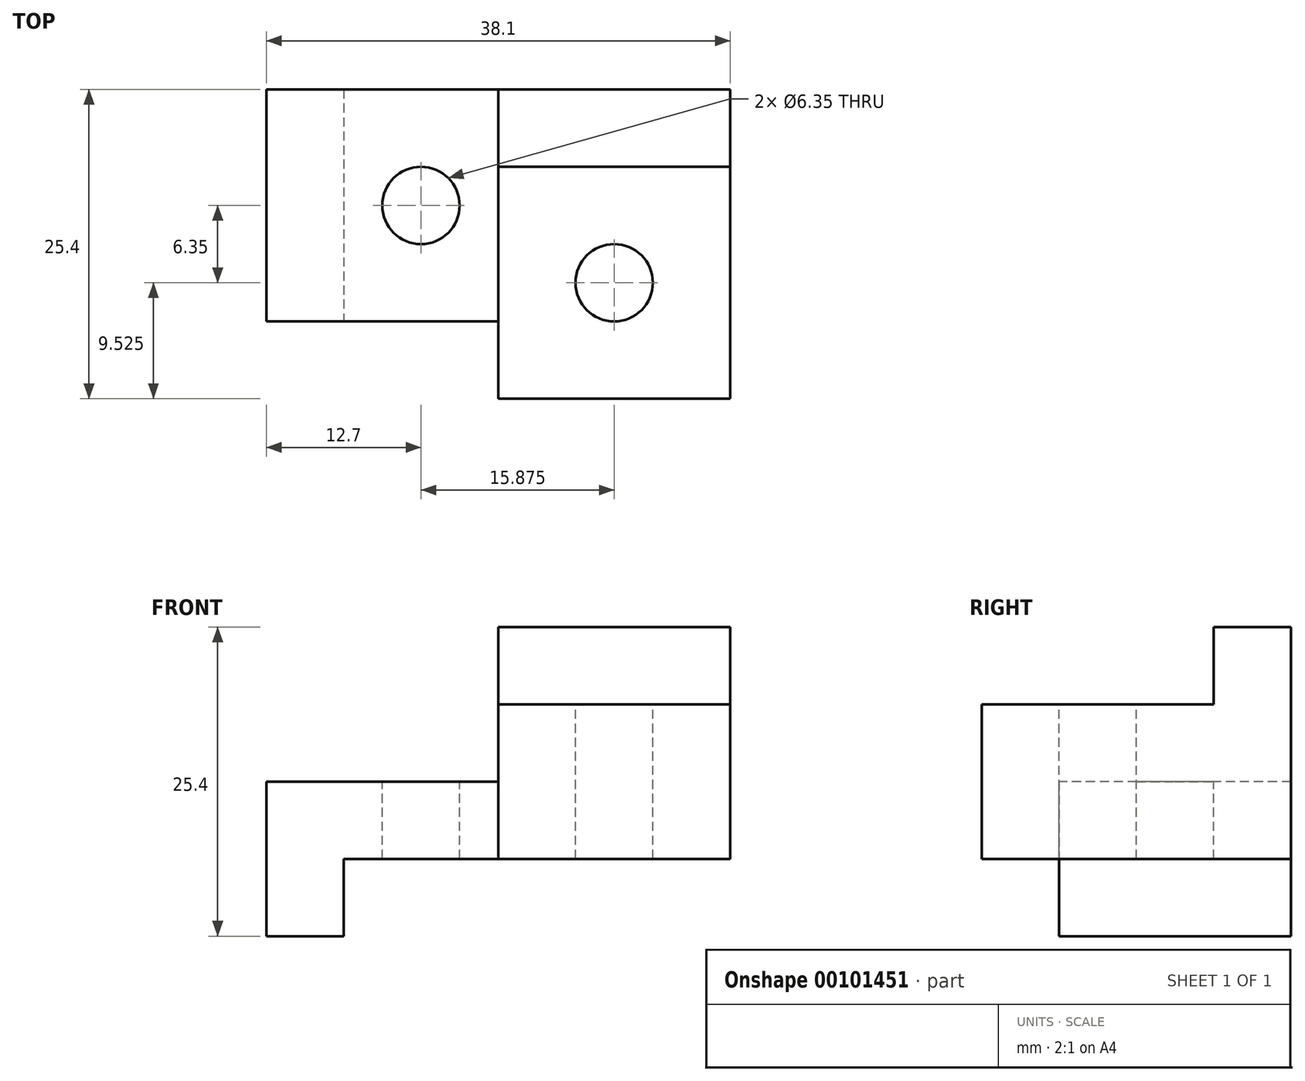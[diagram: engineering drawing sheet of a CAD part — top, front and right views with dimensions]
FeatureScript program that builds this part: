
annotation { "Feature Type Name" : "Feature", "Feature Type Description" : "" }
export const myFeature = defineFeature(function(context is Context, id is Id, definition is map)
    precondition{}
    {
        {
            var Q0;
            Q0=qCreatedBy(makeId("Front.planeOp"),FACE);
            var sketch = newSketch(context, id + "F0", { "sketchPlane" : qUnion([Q0])});
            skLineSegment(sketch, "E0", {"start": v(0, 0) * mm, "end": v(6.35, 0) * mm});
            skLineSegment(sketch, "E1", {"start": v(6.35, 0) * mm, "end": v(6.35, -12.7) * mm});
            skLineSegment(sketch, "E2", {"start": v(6.35, -12.7) * mm, "end": v(0, -12.7) * mm});
            skLineSegment(sketch, "E3", {"start": v(0, -12.7) * mm, "end": v(0, 0) * mm});
            skSolve(sketch);
        }
        {
            var Q0;
            Q0 = qSketchRegion(id + "F0", true);
            extrude(context, id + "F1", {"entities" : qUnion([Q0]), "oppositeDirection" : true, "depth" : 19.05 * mm});
        }
        {
            var Q0;
            Q0=makeQuery(id+"F1.opExtrude","SWEPT_FACE",FACE,{"disambiguationData":[OSD([sQuery(id+"F0.wireOp",EDGE,"E1")])]});
            var sketch = newSketch(context, id + "F2", { "sketchPlane" : qUnion([Q0])});
            skLineSegment(sketch, "E4", {"start": v(19.05, 0) * mm, "end": v(19.05, -6.35) * mm});
            skLineSegment(sketch, "E5", {"start": v(19.05, -6.35) * mm, "end": v(0, -6.35) * mm});
            skLineSegment(sketch, "E6", {"start": v(0, -6.35) * mm, "end": v(0, 0) * mm});
            skLineSegment(sketch, "E7", {"start": v(0, 0) * mm, "end": v(19.05, 0) * mm});
            skSolve(sketch);
        }
        {
            var Q0;
            Q0 = qSketchRegion(id + "F2", true);
            extrude(context, id + "F3", {"entities" : qUnion([Q0]), "operationType" : NewBodyOperationType.ADD, "depth" : 12.7 * mm});
        }
        {
            var Q0;
            Q0=makeQuery(id+"F3.boolean.opBoolean","MERGE",FACE,{"derivedFrom":[makeQuery(id+"F1.opExtrude","SWEPT_FACE",FACE,{"disambiguationData":[OSD([sQuery(id+"F0.wireOp",EDGE,"E0")])]}),makeQuery(id+"F3.opExtrude","SWEPT_FACE",FACE,{"disambiguationData":[OSD([sQuery(id+"F2.wireOp",EDGE,"E7")])]})]});
            var sketch = newSketch(context, id + "F4", { "sketchPlane" : qUnion([Q0])});
            skLineSegment(sketch, "E8", {"start": v(19.05, 19.05) * mm, "end": v(19.05, 9.53) * mm, "construction": true});
            skLineSegment(sketch, "E9", {"start": v(19.05, 9.53) * mm, "end": v(12.7, 9.53) * mm, "construction": true});
            skCircle(sketch, "E10", {"center": v(12.7, 9.53) * mm, "radius": 3.18 * mm});
            skSolve(sketch);
        }
        {
            var Q0;
            Q0 = qSketchRegion(id + "F4", true);
            extrude(context, id + "F5", {"entities" : qUnion([Q0]), "operationType" : NewBodyOperationType.REMOVE, "endBound" : BoundingType.THROUGH_ALL, "oppositeDirection" : true, "depth" : 25.4 * mm});
        }
        {
            var Q0;
            Q0=makeQuery(id+"F3.opExtrude","CAP_FACE",FACE,{"disambiguationData":[OSD([sQuery(id+"F2.wireOp",EDGE,"E4"),sQuery(id+"F2.wireOp",EDGE,"E5"),sQuery(id+"F2.wireOp",EDGE,"E6"),sQuery(id+"F2.wireOp",EDGE,"E7")])],"isStart":false});
            var sketch = newSketch(context, id + "F6", { "sketchPlane" : qUnion([Q0])});
            skLineSegment(sketch, "E11", {"start": v(19.05, -6.35) * mm, "end": v(19.05, 12.7) * mm});
            skPoint(sketch, "E11.endSnap0", {"position": v(19.05, -3.18) * mm});
            skLineSegment(sketch, "E12", {"start": v(19.05, 12.7) * mm, "end": v(12.7, 12.7) * mm});
            skLineSegment(sketch, "E13", {"start": v(12.7, 12.7) * mm, "end": v(12.7, -6.35) * mm});
            skLineSegment(sketch, "E14", {"start": v(12.7, -6.35) * mm, "end": v(19.05, -6.35) * mm});
            skSolve(sketch);
        }
        {
            var Q0;
            Q0 = qSketchRegion(id + "F6", true);
            extrude(context, id + "F7", {"entities" : qUnion([Q0]), "operationType" : NewBodyOperationType.ADD, "depth" : 19.05 * mm});
        }
        {
            var Q0;
            Q0=makeQuery(id+"F7.opExtrude","SWEPT_FACE",FACE,{"disambiguationData":[OSD([sQuery(id+"F6.wireOp",EDGE,"E13")])]});
            var sketch = newSketch(context, id + "F8", { "sketchPlane" : qUnion([Q0])});
            skLineSegment(sketch, "E15", {"start": v(38.1, -6.35) * mm, "end": v(38.1, 6.35) * mm});
            skLineSegment(sketch, "E16", {"start": v(38.1, 6.35) * mm, "end": v(19.05, 6.35) * mm});
            skLineSegment(sketch, "E17", {"start": v(19.05, 6.35) * mm, "end": v(19.05, -6.35) * mm});
            skLineSegment(sketch, "E18", {"start": v(19.05, -6.35) * mm, "end": v(38.1, -6.35) * mm});
            skSolve(sketch);
        }
        {
            var Q0;
            Q0 = qSketchRegion(id + "F8", true);
            extrude(context, id + "F9", {"entities" : qUnion([Q0]), "operationType" : NewBodyOperationType.ADD, "depth" : 19.05 * mm});
        }
        {
            var Q0;
            Q0=makeQuery(id+"F9.opExtrude","SWEPT_FACE",FACE,{"disambiguationData":[OSD([sQuery(id+"F8.wireOp",EDGE,"E16")])]});
            var sketch = newSketch(context, id + "F10", { "sketchPlane" : qUnion([Q0])});
            skLineSegment(sketch, "E19", {"start": v(38.1, 12.7) * mm, "end": v(38.1, 3.17) * mm, "construction": true});
            skLineSegment(sketch, "E20", {"start": v(38.1, 3.17) * mm, "end": v(28.58, 3.17) * mm, "construction": true});
            skLineSegment(sketch, "E21", {"start": v(28.58, 12.7) * mm, "end": v(28.58, 3.17) * mm, "construction": true});
            skCircle(sketch, "E22", {"center": v(28.58, 3.17) * mm, "radius": 3.18 * mm});
            skSolve(sketch);
        }
        {
            var Q0;
            Q0 = qSketchRegion(id + "F10", true);
            extrude(context, id + "F11", {"entities" : qUnion([Q0]), "operationType" : NewBodyOperationType.REMOVE, "endBound" : BoundingType.THROUGH_ALL, "oppositeDirection" : true, "depth" : 25.4 * mm});
        }
    });
